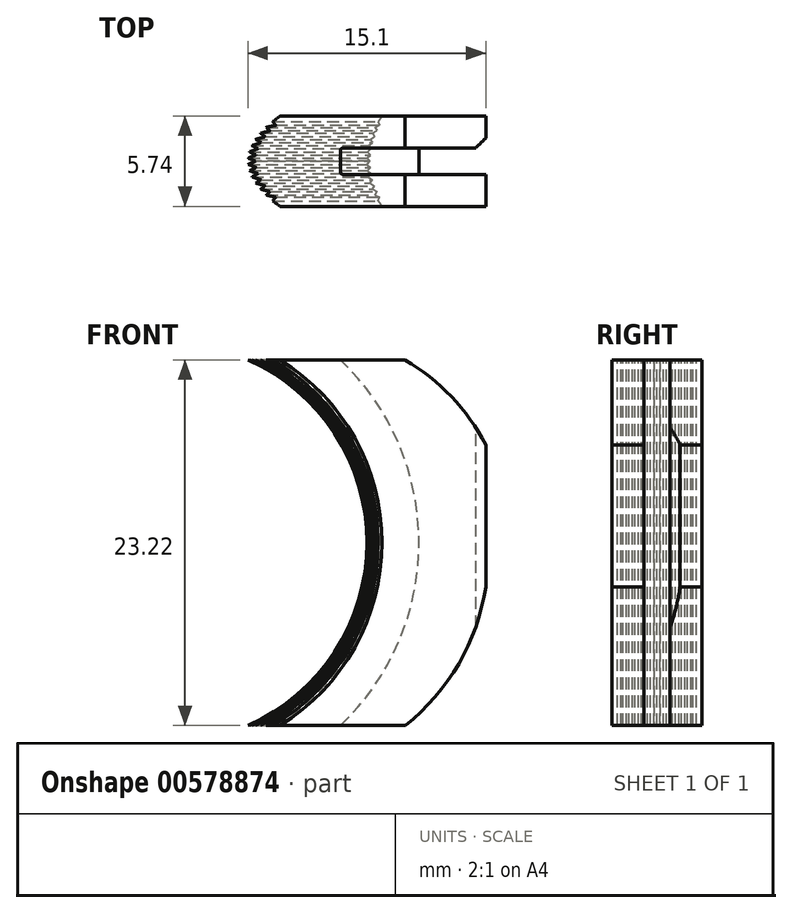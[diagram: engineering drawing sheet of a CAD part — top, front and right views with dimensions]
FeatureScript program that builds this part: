
annotation { "Feature Type Name" : "Feature", "Feature Type Description" : "" }
export const myFeature = defineFeature(function(context is Context, id is Id, definition is map)
    precondition{}
    {
        {
            var Q0;
            Q0=qCreatedBy(makeId("Front.planeOp"),FACE);
            var sketch = newSketch(context, id + "F0", { "sketchPlane" : qUnion([Q0])});
            skLineSegment(sketch, "E0.rect.bottom", {"start": v(0.96, 11.6) * mm, "end": v(10.94, 11.6) * mm});
            skLineSegment(sketch, "E0.rect.top", {"start": v(0.96, -11.6) * mm, "end": v(10.95, -11.6) * mm});
            skLineSegment(sketch, "E0.rect.left", {"start": v(-4.19, 11.6) * mm, "end": v(-4.19, -11.6) * mm, "construction": true});
            skLineSegment(sketch, "E0.rect.right", {"start": v(16.06, 6.22) * mm, "end": v(16.06, -2.8) * mm});
            skPoint(sketch, "E0.rect.middle", {"position": v(5.93, 0) * mm});
            skArc(sketch, "E1", {"start": v(0.96, -11.6) * mm, "mid": v(8.51, 0) * mm, "end": v(0.96, 11.6) * mm});
            skArc(sketch, "E2", {"start": v(16.06, 6.22) * mm, "mid": v(13.87, 9.28) * mm, "end": v(10.94, 11.6) * mm});
            skPoint(sketch, "E3.orphan", {"position": v(16.06, 11.6) * mm});
            skPoint(sketch, "E4.orphan", {"position": v(16.06, -11.6) * mm});
            skArc(sketch, "E5.trimOffspring", {"start": v(10.95, -11.6) * mm, "mid": v(14.34, -7.7) * mm, "end": v(16.06, -2.8) * mm});
            skSolve(sketch);
        }
        {
            var Q0;
            Q0=makeQuery(id+"F0.imprint","IMPRINT",FACE,{"disambiguationData":[TD([[makeQuery(id+"F0.imprint","IMPRINT",EDGE,{"derivedFrom":sQuery(id+"F0.wireOp",EDGE,"E0.rect.bottom")}),-1.0]])]});
            extrude(context, id + "F1", {"entities" : qUnion([Q0]), "endBound" : BoundingType.SYMMETRIC, "depth" : 5.74 * mm});
        }
        {
            var Q0;
            Q0=qCreatedBy(makeId("Front.planeOp"),FACE);
            var sketch = newSketch(context, id + "F2", { "sketchPlane" : qUnion([Q0])});
            skPoint(sketch, "E6.0", {"position": v(-4.19, 0) * mm});
            skArc(sketch, "E7", {"start": v(6.83, -11.6) * mm, "mid": v(11.81, 0) * mm, "end": v(6.83, 11.6) * mm});
            skLineSegment(sketch, "E8.0", {"start": v(6.83, 11.6) * mm, "end": v(10.94, 11.6) * mm});
            skArc(sketch, "E9.0", {"start": v(16.06, 6.22) * mm, "mid": v(13.87, 9.28) * mm, "end": v(10.94, 11.6) * mm});
            skLineSegment(sketch, "E10.0", {"start": v(16.06, 6.22) * mm, "end": v(16.06, -2.8) * mm});
            skArc(sketch, "E11.0", {"start": v(10.95, -11.6) * mm, "mid": v(14.34, -7.7) * mm, "end": v(16.06, -2.8) * mm});
            skLineSegment(sketch, "E12.0", {"start": v(6.83, -11.6) * mm, "end": v(10.95, -11.6) * mm});
            skPoint(sketch, "E13.orphan", {"position": v(0.96, 11.6) * mm});
            skPoint(sketch, "E14.orphan", {"position": v(0.96, -11.6) * mm});
            skSolve(sketch);
        }
        {
            var Q0;
            Q0=makeQuery(id+"F2.imprint","IMPRINT",FACE,{"disambiguationData":[TD([[makeQuery(id+"F2.imprint","IMPRINT",EDGE,{"derivedFrom":sQuery(id+"F2.wireOp",EDGE,"E7")}),-1.0]])]});
            extrude(context, id + "F3", {"entities" : qUnion([Q0]), "operationType" : NewBodyOperationType.REMOVE, "endBound" : BoundingType.SYMMETRIC, "oppositeDirection" : true, "depth" : 1.68 * mm});
        }
        {
            var Q0;
            Q0=makeQuery(id+"F3.boolean.opBoolean","COPY",EDGE,{"derivedFrom":makeQuery(id+"F3.opExtrude","CAP_EDGE",EDGE,{"disambiguationData":[OSD([sQuery(id+"F2.wireOp",EDGE,"E7")])],"isStart":true})});
            var Q1;
            Q1=makeQuery(id+"F3.boolean.opBoolean","COPY",EDGE,{"derivedFrom":makeQuery(id+"F3.opExtrude","CAP_EDGE",EDGE,{"disambiguationData":[OSD([sQuery(id+"F2.wireOp",EDGE,"E7")])],"isStart":false})});
            fillet(context, id + "F4", {"entities" : qUnion([Q0, Q1]), "radius" : 0.13 * mm, "tangentPropagation" : true, "allowEdgeOverflow" : false});
        }
        {
            var Q0;
            Q0=qCreatedBy(makeId("Top.planeOp"),FACE);
            var sketch = newSketch(context, id + "F5", { "sketchPlane" : qUnion([Q0])});
            skLineSegment(sketch, "E15.0", {"start": v(0.96, 2.87) * mm, "end": v(9.47, 2.87) * mm});
            skLineSegment(sketch, "E16.0", {"start": v(0.96, -2.87) * mm, "end": v(0.96, 2.87) * mm});
            skLineSegment(sketch, "E17.0", {"start": v(0.96, -2.87) * mm, "end": v(9.47, -2.87) * mm});
            skLineSegment(sketch, "E18", {"start": v(-4.19, 3.47) * mm, "end": v(-4.19, -3.9) * mm, "construction": true});
            skPoint(sketch, "E19", {"position": v(16.06, 0) * mm});
            skArc(sketch, "E20", {"start": v(9.47, 2.87) * mm, "mid": v(8.5, 0) * mm, "end": v(9.47, -2.87) * mm});
            skPoint(sketch, "E21.orphan", {"position": v(10.94, 2.87) * mm});
            skPoint(sketch, "E22.0.end.orphan", {"position": v(16.06, 2.87) * mm});
            skPoint(sketch, "E23.orphan", {"position": v(16.06, 0.84) * mm});
            skPoint(sketch, "E24.0.end.orphan", {"position": v(16.06, -0.84) * mm});
            skPoint(sketch, "E25.0.start.orphan", {"position": v(16.06, -2.87) * mm});
            skPoint(sketch, "E26.orphan", {"position": v(10.94, -2.87) * mm});
            skPoint(sketch, "E27", {"position": v(8.51, 0) * mm});
            skPoint(sketch, "E28.orphan", {"position": v(8.51, 2.87) * mm});
            skPoint(sketch, "E29.end.orphan", {"position": v(8.51, -2.87) * mm});
            skLineSegment(sketch, "E30", {"start": v(13.28, 0) * mm, "end": v(7.25, 0.53) * mm, "construction": true});
            skLineSegment(sketch, "E31", {"start": v(13.28, 0) * mm, "end": v(7.28, 1.06) * mm, "construction": true});
            skLineSegment(sketch, "E32", {"start": v(13.28, 0) * mm, "end": v(7.48, 1.55) * mm, "construction": true});
            skLineSegment(sketch, "E33", {"start": v(7.7, 2.03) * mm, "end": v(13.28, 0) * mm, "construction": true});
            skLineSegment(sketch, "E34", {"start": v(13.28, 0) * mm, "end": v(8.07, 2.43) * mm, "construction": true});
            skLineSegment(sketch, "E35", {"start": v(8.4, 2.82) * mm, "end": v(13.28, 0) * mm, "construction": true});
            skLineSegment(sketch, "E36", {"start": v(8.71, 0) * mm, "end": v(8.51, 0.2) * mm});
            skLineSegment(sketch, "E37", {"start": v(8.51, 0.2) * mm, "end": v(8.73, 0.4) * mm});
            skLineSegment(sketch, "E38", {"start": v(8.73, 0.4) * mm, "end": v(8.54, 0.6) * mm});
            skLineSegment(sketch, "E39", {"start": v(8.54, 0.6) * mm, "end": v(8.78, 0.8) * mm});
            skLineSegment(sketch, "E40", {"start": v(8.78, 0.8) * mm, "end": v(8.61, 1) * mm});
            skLineSegment(sketch, "E41", {"start": v(8.61, 1) * mm, "end": v(8.87, 1.18) * mm});
            skLineSegment(sketch, "E42", {"start": v(8.87, 1.18) * mm, "end": v(8.71, 1.39) * mm});
            skLineSegment(sketch, "E43", {"start": v(8.71, 1.39) * mm, "end": v(8.99, 1.56) * mm});
            skLineSegment(sketch, "E44", {"start": v(8.99, 1.56) * mm, "end": v(8.85, 1.78) * mm});
            skLineSegment(sketch, "E45", {"start": v(8.85, 1.78) * mm, "end": v(9.14, 1.93) * mm});
            skLineSegment(sketch, "E46", {"start": v(9.14, 1.93) * mm, "end": v(9.02, 2.15) * mm});
            skLineSegment(sketch, "E47", {"start": v(9.02, 2.15) * mm, "end": v(9.32, 2.29) * mm});
            skLineSegment(sketch, "E48", {"start": v(9.32, 2.29) * mm, "end": v(9.22, 2.51) * mm});
            skLineSegment(sketch, "E49", {"start": v(13.28, 0) * mm, "end": v(7.17, -0.53) * mm, "construction": true});
            skLineSegment(sketch, "E50", {"start": v(13.28, 0) * mm, "end": v(7.21, -1.07) * mm, "construction": true});
            skLineSegment(sketch, "E51", {"start": v(7.37, -1.58) * mm, "end": v(13.28, 0) * mm, "construction": true});
            skLineSegment(sketch, "E52", {"start": v(13.28, 0) * mm, "end": v(7.59, -2.07) * mm, "construction": true});
            skLineSegment(sketch, "E53", {"start": v(7.86, -2.53) * mm, "end": v(13.28, 0) * mm, "construction": true});
            skLineSegment(sketch, "E54", {"start": v(13.28, 0) * mm, "end": v(8.15, -2.96) * mm, "construction": true});
            skLineSegment(sketch, "E55", {"start": v(8.5, -3.35) * mm, "end": v(13.28, 0) * mm, "construction": true});
            skLineSegment(sketch, "E56", {"start": v(8.71, 0) * mm, "end": v(8.51, -0.2) * mm});
            skLineSegment(sketch, "E57", {"start": v(8.51, -0.2) * mm, "end": v(8.73, -0.4) * mm});
            skLineSegment(sketch, "E58", {"start": v(8.73, -0.4) * mm, "end": v(8.54, -0.6) * mm});
            skLineSegment(sketch, "E59", {"start": v(8.54, -0.6) * mm, "end": v(8.78, -0.8) * mm});
            skLineSegment(sketch, "E60", {"start": v(8.78, -0.8) * mm, "end": v(8.61, -1) * mm});
            skLineSegment(sketch, "E61", {"start": v(8.61, -1) * mm, "end": v(8.87, -1.18) * mm});
            skLineSegment(sketch, "E62", {"start": v(8.87, -1.18) * mm, "end": v(8.71, -1.39) * mm});
            skLineSegment(sketch, "E63", {"start": v(8.71, -1.39) * mm, "end": v(8.99, -1.56) * mm});
            skLineSegment(sketch, "E64", {"start": v(8.99, -1.56) * mm, "end": v(8.85, -1.78) * mm});
            skLineSegment(sketch, "E65", {"start": v(8.85, -1.78) * mm, "end": v(9.14, -1.93) * mm});
            skLineSegment(sketch, "E66", {"start": v(9.14, -1.93) * mm, "end": v(9.02, -2.15) * mm});
            skLineSegment(sketch, "E67", {"start": v(9.02, -2.15) * mm, "end": v(9.32, -2.29) * mm});
            skLineSegment(sketch, "E68", {"start": v(9.32, -2.29) * mm, "end": v(9.22, -2.51) * mm});
            skSolve(sketch);
        }
        {
            var Q0;
            Q0=qSketchRegion(id+"F5",true);
            var Q1;
            Q1=sQuery(id+"F5.wireOp",EDGE,"E18");
            revolve(context, id + "F6", {"operationType" : NewBodyOperationType.REMOVE, "entities" : qUnion([Q0]), "axis" : qUnion([Q1]), "revolveType" : RevolveType.FULL, "oppositeDirection" : true});
        }
        {
            var Q0;
            Q0=makeQuery(id+"F3.boolean.opBoolean","COPY",EDGE,{"derivedFrom":makeQuery(id+"F3.opExtrude","CAP_EDGE",EDGE,{"disambiguationData":[OSD([sQuery(id+"F2.wireOp",EDGE,"E10.0")])],"isStart":false})});
            var Q1;
            Q1=makeQuery(id+"F3.boolean.opBoolean","COPY",EDGE,{"derivedFrom":makeQuery(id+"F3.opExtrude","CAP_EDGE",EDGE,{"disambiguationData":[OSD([sQuery(id+"F2.wireOp",EDGE,"E10.0")])],"isStart":true})});
            chamfer(context, id + "F7", {"entities" : qUnion([Q0, Q1]), "width" : 0.64 * mm, "tangentPropagation" : true});
        }
    });
